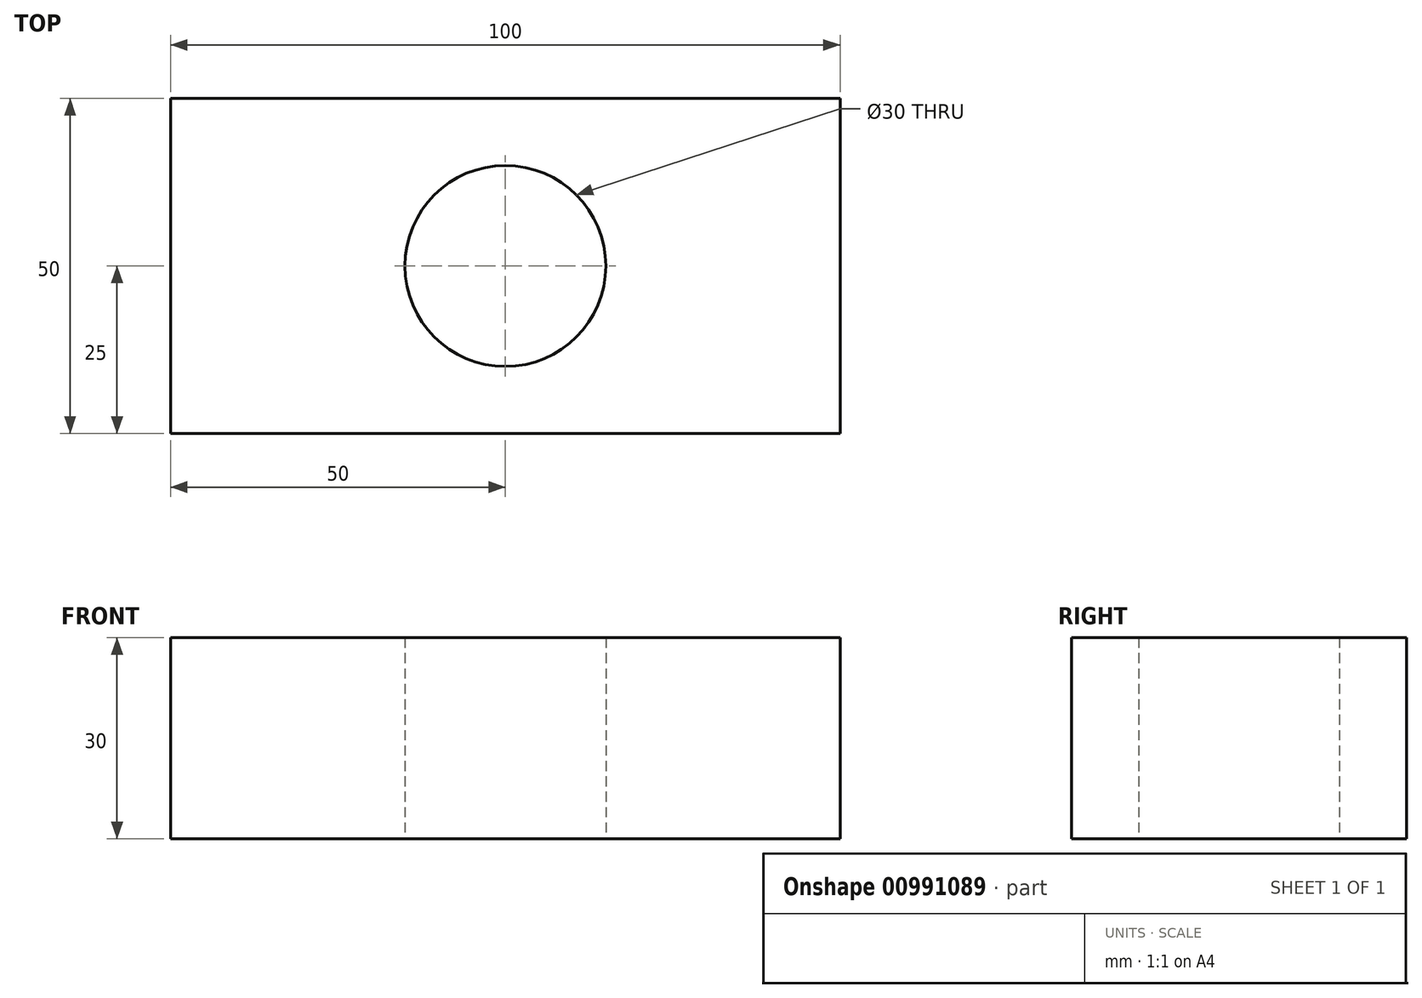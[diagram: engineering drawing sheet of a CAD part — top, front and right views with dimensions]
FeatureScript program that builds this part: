
annotation { "Feature Type Name" : "Feature", "Feature Type Description" : "" }
export const myFeature = defineFeature(function(context is Context, id is Id, definition is map)
    precondition{}
    {
        {
            var Q0;
            Q0=qCreatedBy(makeId("Top.planeOp"),FACE);
            var sketch = newSketch(context, id + "F0", { "sketchPlane" : qUnion([Q0])});
            skLineSegment(sketch, "E0.bottom", {"start": v(50, -25) * mm, "end": v(-50, -25) * mm});
            skLineSegment(sketch, "E0.top", {"start": v(50, 25) * mm, "end": v(-50, 25) * mm});
            skLineSegment(sketch, "E0.left", {"start": v(50, -25) * mm, "end": v(50, 25) * mm});
            skLineSegment(sketch, "E0.right", {"start": v(-50, -25) * mm, "end": v(-50, 25) * mm});
            skPoint(sketch, "E0.middle", {"position": v(0, 0) * mm});
            skCircle(sketch, "E1", {"center": v(0, 0) * mm, "radius": 15 * mm});
            skSolve(sketch);
        }
        {
            var Q0;
            Q0=makeQuery(id+"F0.imprint","IMPRINT",FACE,{"disambiguationData":[TD([[makeQuery(id+"F0.imprint","IMPRINT",EDGE,{"derivedFrom":sQuery(id+"F0.wireOp",EDGE,"E0.bottom")}),-1.0]])]});
            extrude(context, id + "F1", {"entities" : qUnion([Q0]), "depth" : 30 * mm, "offsetDistance" : 25 * mm});
        }
    });
